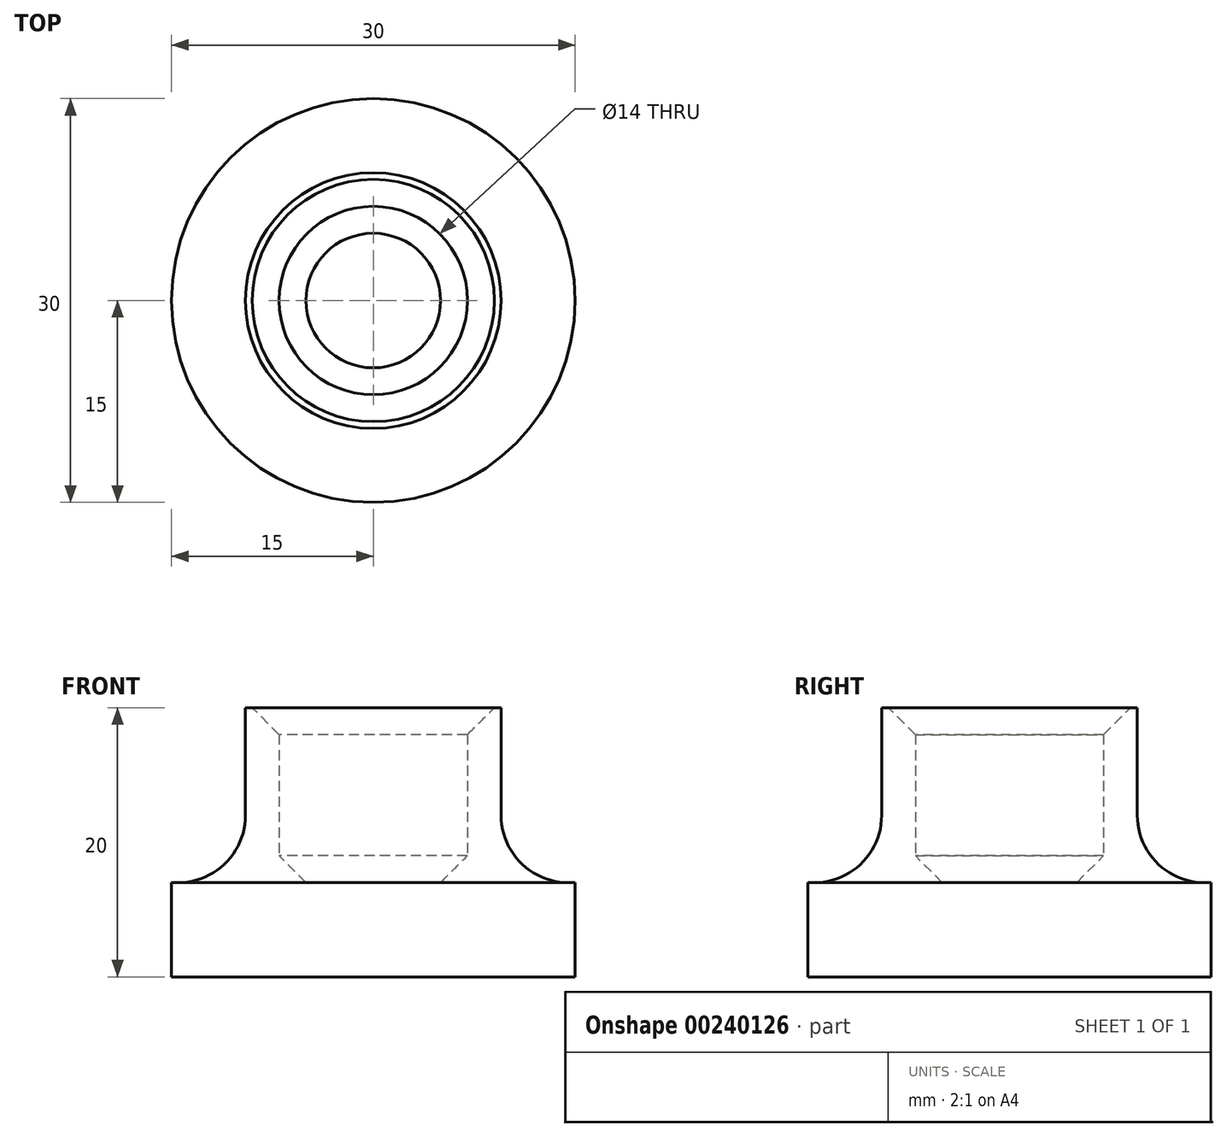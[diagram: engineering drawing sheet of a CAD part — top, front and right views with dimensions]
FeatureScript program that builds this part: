
annotation { "Feature Type Name" : "Feature", "Feature Type Description" : "" }
export const myFeature = defineFeature(function(context is Context, id is Id, definition is map)
    precondition{}
    {
        {
            var Q0;
            Q0=qCreatedBy(makeId("Top.planeOp"),FACE);
            var sketch = newSketch(context, id + "F0", { "sketchPlane" : qUnion([Q0])});
            skCircle(sketch, "E0", {"center": v(0, 0) * mm, "radius": 7 * mm});
            skCircle(sketch, "E1", {"center": v(0, 0) * mm, "radius": 9.5 * mm});
            skCircle(sketch, "E2", {"center": v(0, 0) * mm, "radius": 15 * mm});
            skSolve(sketch);
        }
        {
            var Q0;
            Q0=makeQuery(id+"F0.imprint","IMPRINT",FACE,{"disambiguationData":[TD([[makeQuery(id+"F0.imprint","IMPRINT",EDGE,{"derivedFrom":sQuery(id+"F0.wireOp",EDGE,"E1")}),-1.0]])]});
            var Q1;
            Q1=makeQuery(id+"F0.imprint","IMPRINT",FACE,{"disambiguationData":[TD([[makeQuery(id+"F0.imprint","IMPRINT",EDGE,{"derivedFrom":sQuery(id+"F0.wireOp",EDGE,"E0")}),-1.0]])]});
            var Q2;
            Q2=makeQuery(id+"F0.imprint","IMPRINT",FACE,{"disambiguationData":[TD([[makeQuery(id+"F0.imprint","IMPRINT",EDGE,{"derivedFrom":sQuery(id+"F0.wireOp",EDGE,"E0")}),1.0]])]});
            extrude(context, id + "F1", {"entities" : qUnion([Q0, Q1, Q2]), "depth" : 7 * mm});
        }
        {
            var Q0;
            Q0=makeQuery(id+"F0.imprint","IMPRINT",FACE,{"disambiguationData":[TD([[makeQuery(id+"F0.imprint","IMPRINT",EDGE,{"derivedFrom":sQuery(id+"F0.wireOp",EDGE,"E0")}),-1.0]])]});
            extrude(context, id + "F2", {"entities" : qUnion([Q0]), "operationType" : NewBodyOperationType.ADD, "depth" : 20 * mm});
        }
        {
            var Q0;
            Q0=makeQuery(id+"F2.boolean.opBoolean","INTERSECT",EDGE,{"derivedFrom":[makeQuery(id+"F1.opExtrude","CAP_FACE",FACE,{"disambiguationData":[OSD([sQuery(id+"F0.wireOp",EDGE,"E2")])],"isStart":false}),makeQuery(id+"F2.opExtrude","SWEPT_FACE",FACE,{"disambiguationData":[OSD([sQuery(id+"F0.wireOp",EDGE,"E1")])]})]});
            fillet(context, id + "F3", {"entities" : qUnion([Q0]), "radius" : 5 * mm, "tangentPropagation" : true, "allowEdgeOverflow" : false});
        }
        {
            var Q0;
            Q0=makeQuery(id+"F2.opExtrude","CAP_EDGE",EDGE,{"disambiguationData":[OSD([sQuery(id+"F0.wireOp",EDGE,"E0")])],"isStart":false});
            chamfer(context, id + "F4", {"entities" : qUnion([Q0]), "width" : 2 * mm, "tangentPropagation" : true});
        }
        {
            var Q0;
            Q0=makeQuery(id+"F2.boolean.opBoolean","INTERSECT",EDGE,{"derivedFrom":[makeQuery(id+"F1.opExtrude","CAP_FACE",FACE,{"disambiguationData":[OSD([sQuery(id+"F0.wireOp",EDGE,"E2")])],"isStart":false}),makeQuery(id+"F2.opExtrude","SWEPT_FACE",FACE,{"disambiguationData":[OSD([sQuery(id+"F0.wireOp",EDGE,"E0")])]})]});
            chamfer(context, id + "F5", {"entities" : qUnion([Q0]), "width" : 2 * mm, "tangentPropagation" : true});
        }
    });
